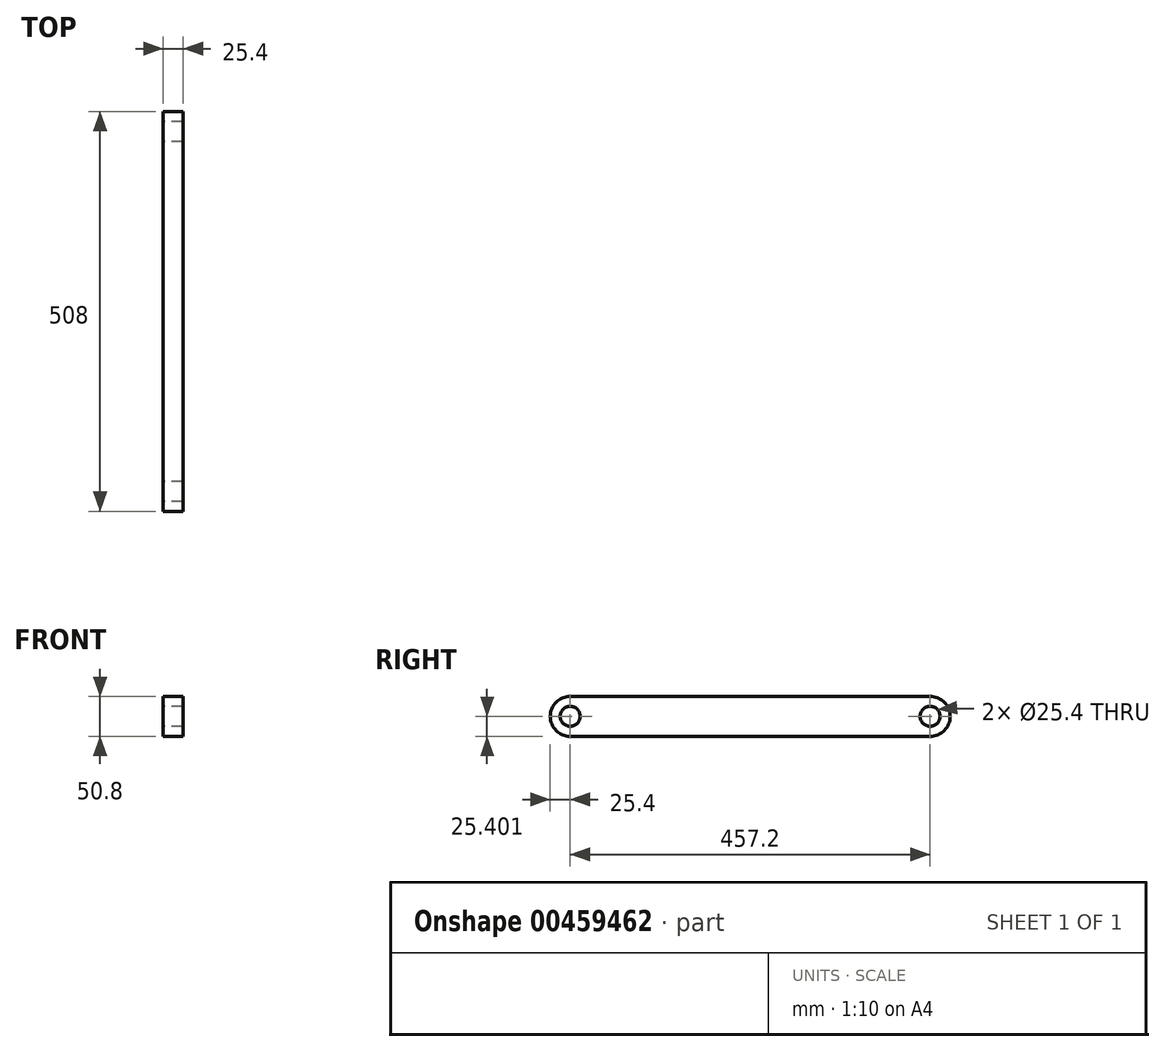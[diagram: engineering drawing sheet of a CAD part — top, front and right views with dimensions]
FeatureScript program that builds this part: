
annotation { "Feature Type Name" : "Feature", "Feature Type Description" : "" }
export const myFeature = defineFeature(function(context is Context, id is Id, definition is map)
    precondition{}
    {
        {
            var Q0;
            Q0=qCreatedBy(makeId("Right.planeOp"),FACE);
            var sketch = newSketch(context, id + "F0", { "sketchPlane" : qUnion([Q0])});
            skLineSegment(sketch, "E0.bottom", {"start": v(-63.06, 20.65) * mm, "end": v(394.14, 20.65) * mm});
            skLineSegment(sketch, "E0.top", {"start": v(-63.06, -30.15) * mm, "end": v(394.14, -30.15) * mm});
            skLineSegment(sketch, "E0.left", {"start": v(-63.06, 20.65) * mm, "end": v(-63.06, -30.15) * mm});
            skLineSegment(sketch, "E0.right", {"start": v(394.14, 20.65) * mm, "end": v(394.14, -30.15) * mm});
            skCircle(sketch, "E1", {"center": v(-63.06, -4.75) * mm, "radius": 25.4 * mm});
            skCircle(sketch, "E2", {"center": v(-63.06, -4.75) * mm, "radius": 12.7 * mm});
            skCircle(sketch, "E3", {"center": v(394.14, -4.75) * mm, "radius": 25.4 * mm});
            skCircle(sketch, "E4", {"center": v(394.14, -4.75) * mm, "radius": 12.7 * mm});
            skSolve(sketch);
        }
        {
            var Q0;
            Q0=qSketchRegion(id+"F0",true);
            extrude(context, id + "F1", {"entities" : qUnion([Q0]), "depth" : 25.4 * mm});
        }
    });
